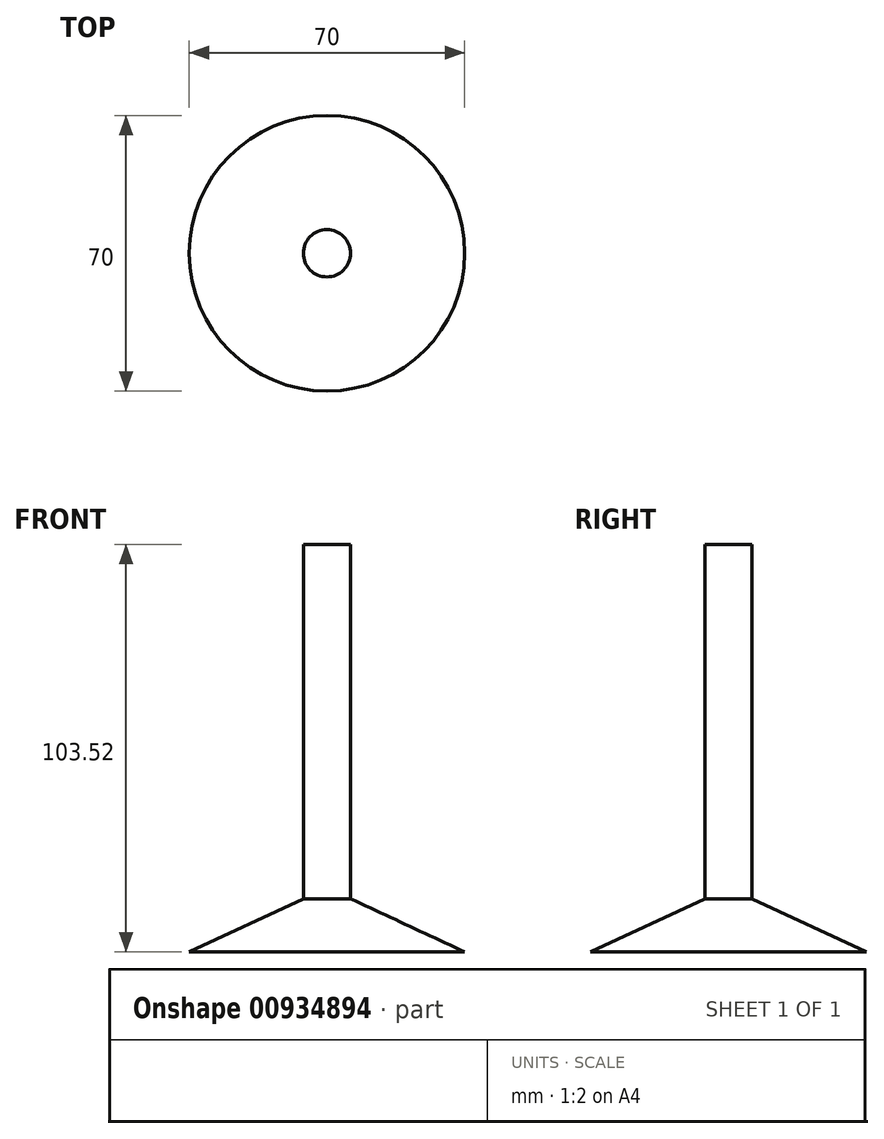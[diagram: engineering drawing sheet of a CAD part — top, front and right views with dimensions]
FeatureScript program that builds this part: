
annotation { "Feature Type Name" : "Feature", "Feature Type Description" : "" }
export const myFeature = defineFeature(function(context is Context, id is Id, definition is map)
    precondition{}
    {
        {
            var Q0;
            Q0=qCreatedBy(makeId("Front.planeOp"),FACE);
            var sketch = newSketch(context, id + "F0", { "sketchPlane" : qUnion([Q0])});
            skLineSegment(sketch, "E0", {"start": v(0, 42.67) * mm, "end": v(0, -60.85) * mm});
            skLineSegment(sketch, "E1", {"start": v(0, -60.85) * mm, "end": v(35, -60.85) * mm});
            skLineSegment(sketch, "E2", {"start": v(35, -60.85) * mm, "end": v(6, -47.33) * mm});
            skLineSegment(sketch, "E3", {"start": v(6, -47.33) * mm, "end": v(6, 42.67) * mm});
            skLineSegment(sketch, "E4", {"start": v(6, 42.67) * mm, "end": v(0, 42.67) * mm});
            skSolve(sketch);
        }
        {
            var Q0;
            Q0=makeQuery(id+"F0.imprint","IMPRINT",FACE,{"disambiguationData":[TD([[makeQuery(id+"F0.imprint","IMPRINT",EDGE,{"derivedFrom":sQuery(id+"F0.wireOp",EDGE,"E0")}),1.0]])]});
            var Q1;
            Q1=sQuery(id+"F0.wireOp",EDGE,"E0");
            revolve(context, id + "F1", {"surfaceOperationType" : NewSurfaceOperationType.NEW, "entities" : qUnion([Q0]), "axis" : qUnion([Q1]), "revolveType" : RevolveType.FULL});
        }
    });
